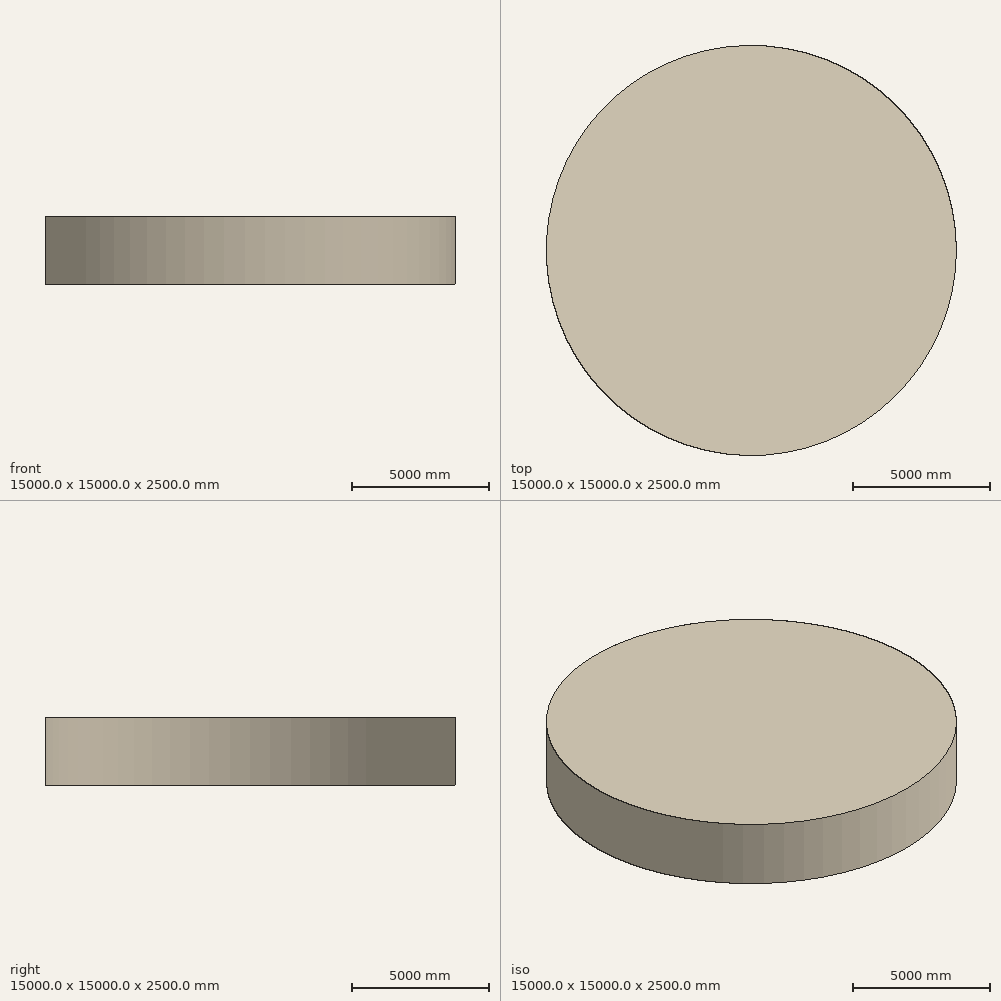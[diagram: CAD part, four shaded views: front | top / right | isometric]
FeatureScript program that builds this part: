
annotation { "Feature Type Name" : "Feature", "Feature Type Description" : "" }
export const myFeature = defineFeature(function(context is Context, id is Id, definition is map)
    precondition{}
    {
        {
            var Q0;
            Q0=qCreatedBy(makeId("Top.planeOp"),FACE);
            var sketch = newSketch(context, id + "F0", { "sketchPlane" : qUnion([Q0])});
            skCircle(sketch, "E0", {"center": v(0, 0) * mm, "radius": 7500 * mm});
            skSolve(sketch);
        }
        {
            var Q0;
            Q0=makeQuery(id+"F0.imprint","IMPRINT",FACE,{"disambiguationData":[TD([[makeQuery(id+"F0.imprint","IMPRINT",EDGE,{"derivedFrom":sQuery(id+"F0.wireOp",EDGE,"E0")}),1.0]])]});
            extrude(context, id + "F1", {"entities" : qUnion([Q0]), "depth" : 2500 * mm, "offsetDistance" : 25 * mm});
        }
    });
